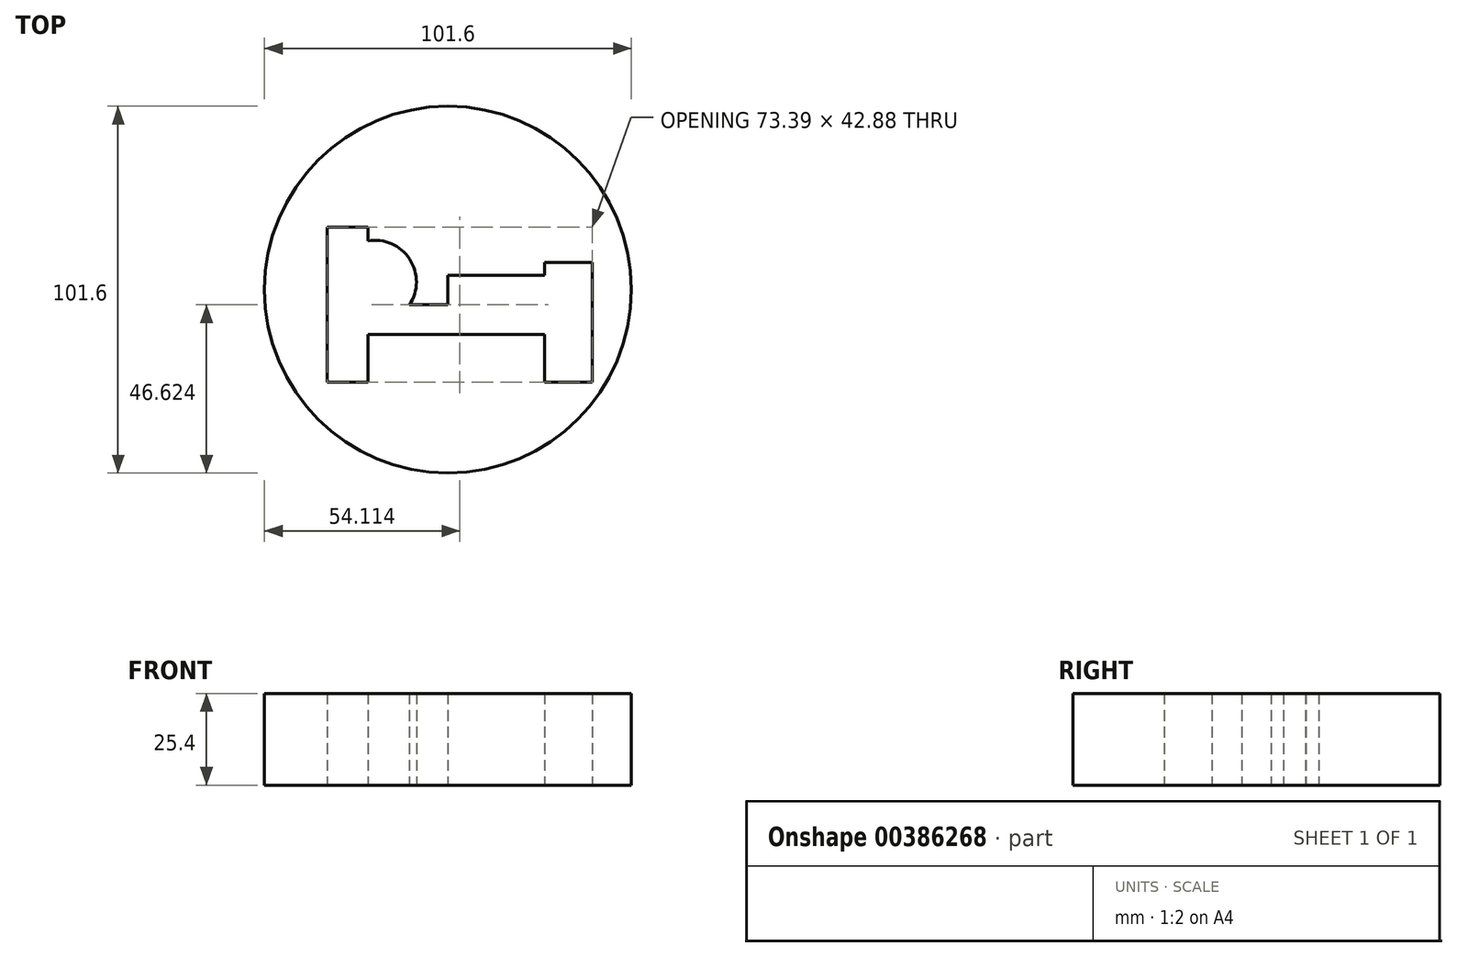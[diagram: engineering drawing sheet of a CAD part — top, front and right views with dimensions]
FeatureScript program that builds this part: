
annotation { "Feature Type Name" : "Feature", "Feature Type Description" : "" }
export const myFeature = defineFeature(function(context is Context, id is Id, definition is map)
    precondition{}
    {
        {
            var Q0;
            Q0=qCreatedBy(makeId("Top.planeOp"),FACE);
            var sketch = newSketch(context, id + "F0", { "sketchPlane" : qUnion([Q0])});
            skCircle(sketch, "E0", {"center": v(-14.97, 9.5) * mm, "radius": 50.8 * mm});
            skLineSegment(sketch, "E1", {"start": v(-48.35, -16.12) * mm, "end": v(-37.13, -16.12) * mm});
            skLineSegment(sketch, "E2", {"start": v(-37.13, -16.12) * mm, "end": v(-37.13, -2.88) * mm});
            skLineSegment(sketch, "E3", {"start": v(-37.13, 26.77) * mm, "end": v(-48.35, 26.77) * mm});
            skLineSegment(sketch, "E4", {"start": v(-48.35, 26.77) * mm, "end": v(-48.35, -16.12) * mm});
            skLineSegment(sketch, "E5", {"start": v(-37.13, -2.88) * mm, "end": v(11.8, -2.88) * mm});
            skLineSegment(sketch, "E6", {"start": v(11.8, -2.88) * mm, "end": v(11.8, -16.12) * mm});
            skLineSegment(sketch, "E7", {"start": v(11.8, -16.12) * mm, "end": v(25.04, -16.12) * mm});
            skLineSegment(sketch, "E8", {"start": v(25.04, -16.12) * mm, "end": v(25.04, 16.98) * mm});
            skLineSegment(sketch, "E9", {"start": v(25.04, 16.98) * mm, "end": v(11.8, 16.98) * mm});
            skLineSegment(sketch, "E10", {"start": v(11.8, 16.98) * mm, "end": v(11.8, 5.32) * mm});
            skLineSegment(sketch, "E11", {"start": v(-37.13, 5.32) * mm, "end": v(11.8, 5.32) * mm});
            skLineSegment(sketch, "E12", {"start": v(11.8, 5.32) * mm, "end": v(9.79, 6.04) * mm});
            skLineSegment(sketch, "E13.trimOffspring", {"start": v(-37.13, 5.32) * mm, "end": v(-37.13, 26.77) * mm});
            skLineSegment(sketch, "E14", {"start": v(-37.13, 16.05) * mm, "end": v(-25.61, 5.32) * mm});
            skArc(sketch, "E15", {"start": v(-25.61, 5.32) * mm, "mid": v(-25.56, 17.95) * mm, "end": v(-37.13, 23.02) * mm});
            skLineSegment(sketch, "E16.bottom", {"start": v(-14.97, 9.5) * mm, "end": v(11.8, 9.5) * mm});
            skLineSegment(sketch, "E16.top", {"start": v(-14.97, 5.32) * mm, "end": v(11.8, 5.32) * mm});
            skLineSegment(sketch, "E16.left", {"start": v(-14.97, 9.5) * mm, "end": v(-14.97, 5.32) * mm});
            skLineSegment(sketch, "E16.right", {"start": v(11.8, 9.5) * mm, "end": v(11.8, 5.32) * mm});
            skLineSegment(sketch, "E17.bottom", {"start": v(11.8, 9.5) * mm, "end": v(-14.97, 9.5) * mm});
            skLineSegment(sketch, "E17.top", {"start": v(11.8, 13.53) * mm, "end": v(-14.97, 13.53) * mm});
            skLineSegment(sketch, "E17.left", {"start": v(11.8, 9.5) * mm, "end": v(11.8, 13.53) * mm});
            skLineSegment(sketch, "E17.right", {"start": v(-14.97, 9.5) * mm, "end": v(-14.97, 13.53) * mm});
            skSolve(sketch);
        }
        {
            var Q0;
            Q0 = qSketchRegion(id + "F0", true);
            extrude(context, id + "F1", {"entities" : qUnion([Q0]), "depth" : 25.4 * mm});
        }
        {
            var Q0;
            Q0 = qSketchRegion(id + "F0", true);
            extrude(context, id + "F2", {"entities" : qUnion([Q0]), "operationType" : NewBodyOperationType.ADD, "depth" : 25.4 * mm});
        }
    });
